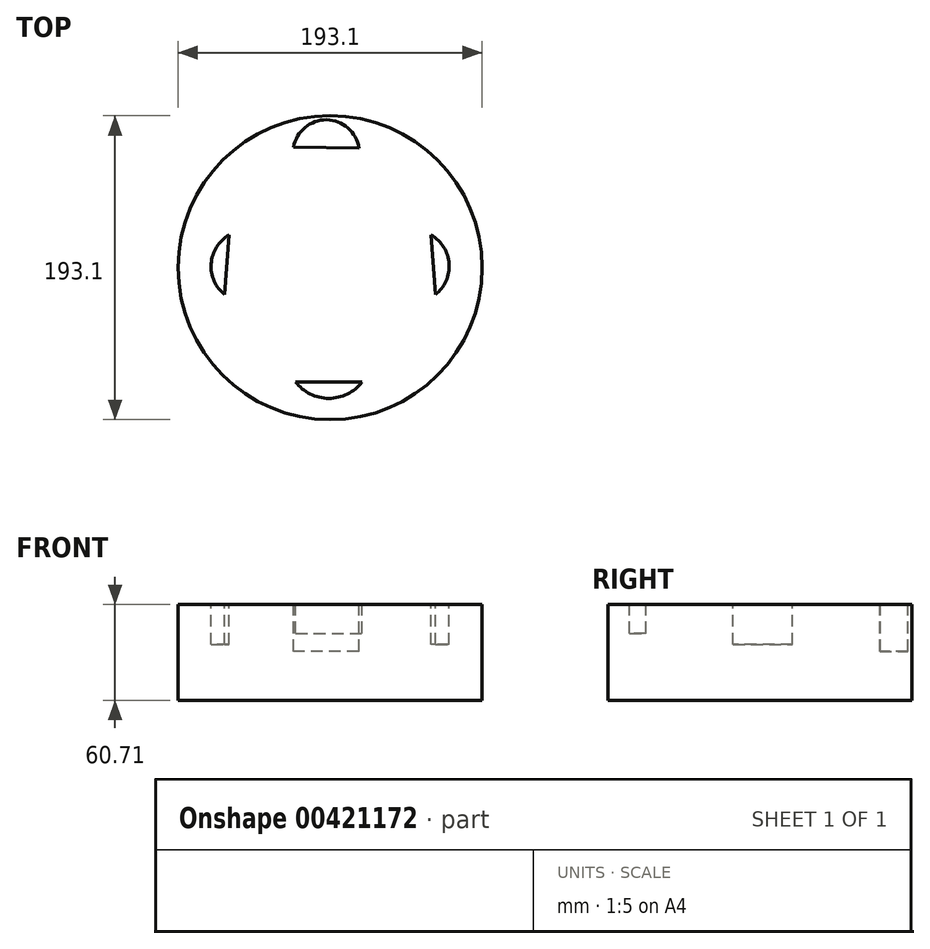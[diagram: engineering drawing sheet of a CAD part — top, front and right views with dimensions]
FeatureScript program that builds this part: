
annotation { "Feature Type Name" : "Feature", "Feature Type Description" : "" }
export const myFeature = defineFeature(function(context is Context, id is Id, definition is map)
    precondition{}
    {
        {
            var Q0;
            Q0=qCreatedBy(makeId("Top.planeOp"),FACE);
            var sketch = newSketch(context, id + "F0", { "sketchPlane" : qUnion([Q0])});
            skCircle(sketch, "E0", {"center": v(0, 0) * mm, "radius": 96.55 * mm});
            skSolve(sketch);
        }
        {
            var Q0;
            Q0=makeQuery(id+"F0.imprint","IMPRINT",FACE,{"disambiguationData":[TD([[makeQuery(id+"F0.imprint","IMPRINT",EDGE,{"derivedFrom":sQuery(id+"F0.wireOp",EDGE,"E0")}),1.0]])]});
            extrude(context, id + "F1", {"entities" : qUnion([Q0]), "oppositeDirection" : true, "depth" : 60.7 * mm});
        }
        {
            var Q0;
            Q0=makeQuery(id+"F1.opExtrude","CAP_FACE",FACE,{"disambiguationData":[OSD([sQuery(id+"F0.wireOp",EDGE,"E0")])],"isStart":true});
            var sketch = newSketch(context, id + "F2", { "sketchPlane" : qUnion([Q0])});
            skLineSegment(sketch, "E1", {"start": v(-96.55, 0) * mm, "end": v(0, 0) * mm});
            skLineSegment(sketch, "E2", {"start": v(0, 0) * mm, "end": v(96.55, 0) * mm});
            skLineSegment(sketch, "E3", {"start": v(0, 0) * mm, "end": v(0, 96.55) * mm});
            skLineSegment(sketch, "E4", {"start": v(0, 0) * mm, "end": v(0, -96.55) * mm});
            skSolve(sketch);
        }
        {
            var Q0;
            {var subQ0=sQuery(id+"F2.wireOp",EDGE,"E2");Q0=makeQuery(id+"F2.imprint","IMPRINT",FACE,{"disambiguationData":[TD([[makeQuery(id+"F2.imprint","IMPRINT",EDGE,{"derivedFrom":subQ0}),-1.0]])]});}
            var sketch = newSketch(context, id + "F3", { "sketchPlane" : qUnion([Q0])});
            skArc(sketch, "E5", {"start": v(-21.94, -72.5) * mm, "mid": v(-0.85, -83) * mm, "end": v(20.3, -72.63) * mm});
            skLineSegment(sketch, "E6", {"start": v(-21.94, -72.5) * mm, "end": v(20.3, -72.63) * mm});
            skSolve(sketch);
        }
        {
            var Q0;
            {var subQ0=sQuery(id+"F3.wireOp",EDGE,"E6");var subQ1=sQuery(id+"F3.wireOp",EDGE,"E5");var subQ2=makeQuery(id+"F3.imprint","INTERSECT",VERTEX,{"disambiguationData":[OD(1.0)],"derivedFrom":[subQ1,subQ0]});Q0=makeQuery(id+"F3.imprint","IMPRINT",FACE,{"disambiguationData":[TD([[makeQuery(id+"F3.imprint","IMPRINT",EDGE,{"disambiguationData":[TD([[subQ2,1.0]])],"derivedFrom":subQ1}),1.0]])]});}
            extrude(context, id + "F4", {"entities" : qUnion([Q0]), "operationType" : NewBodyOperationType.REMOVE, "oppositeDirection" : true, "depth" : 16.76 * mm});
        }
        {
            var Q0;
            Q0 = qSketchRegion(id + "F3", true);
            extrude(context, id + "F5", {"entities" : qUnion([Q0]), "operationType" : NewBodyOperationType.REMOVE, "oppositeDirection" : true, "depth" : 18.29 * mm});
        }
        {
            var Q0;
            Q0=qCreatedBy(makeId("Top.planeOp"),FACE);
            var sketch = newSketch(context, id + "F6", { "sketchPlane" : qUnion([Q0])});
            skLineSegment(sketch, "E7", {"start": v(18.26, 76.04) * mm, "end": v(-23.17, 76.51) * mm});
            skArc(sketch, "E8", {"start": v(18.26, 76.04) * mm, "mid": v(-2.26, 93.92) * mm, "end": v(-23.17, 76.51) * mm});
            skSolve(sketch);
        }
        {
            var Q0;
            Q0 = qSketchRegion(id + "F6", true);
            extrude(context, id + "F7", {"entities" : qUnion([Q0]), "operationType" : NewBodyOperationType.REMOVE, "oppositeDirection" : true, "depth" : 29.72 * mm});
        }
        {
            var Q0;
            Q0=qCreatedBy(makeId("Top.planeOp"),FACE);
            var sketch = newSketch(context, id + "F8", { "sketchPlane" : qUnion([Q0])});
            skArc(sketch, "E9", {"start": v(66.9, -17.18) * mm, "mid": v(75.55, 2.46) * mm, "end": v(64.24, 20.7) * mm});
            skLineSegment(sketch, "E10", {"start": v(66.9, -17.18) * mm, "end": v(64.24, 20.7) * mm});
            skArc(sketch, "E11.MirrorCS", {"start": v(-66.9, -17.18) * mm, "mid": v(-75.55, 2.46) * mm, "end": v(-64.24, 20.7) * mm});
            skLineSegment(sketch, "E12.MirrorCS", {"start": v(-66.9, -17.18) * mm, "end": v(-64.24, 20.7) * mm});
            skSolve(sketch);
        }
        {
            var Q0;
            Q0 = qSketchRegion(id + "F8", true);
            extrude(context, id + "F9", {"entities" : qUnion([Q0]), "operationType" : NewBodyOperationType.REMOVE, "oppositeDirection" : true, "depth" : 24.9 * mm});
        }
        {
            var Q0;
            Q0 = qSketchRegion(id + "F8", true);
            extrude(context, id + "F10", {"entities" : qUnion([Q0]), "operationType" : NewBodyOperationType.REMOVE, "oppositeDirection" : true, "depth" : 25.4 * mm});
        }
    });
